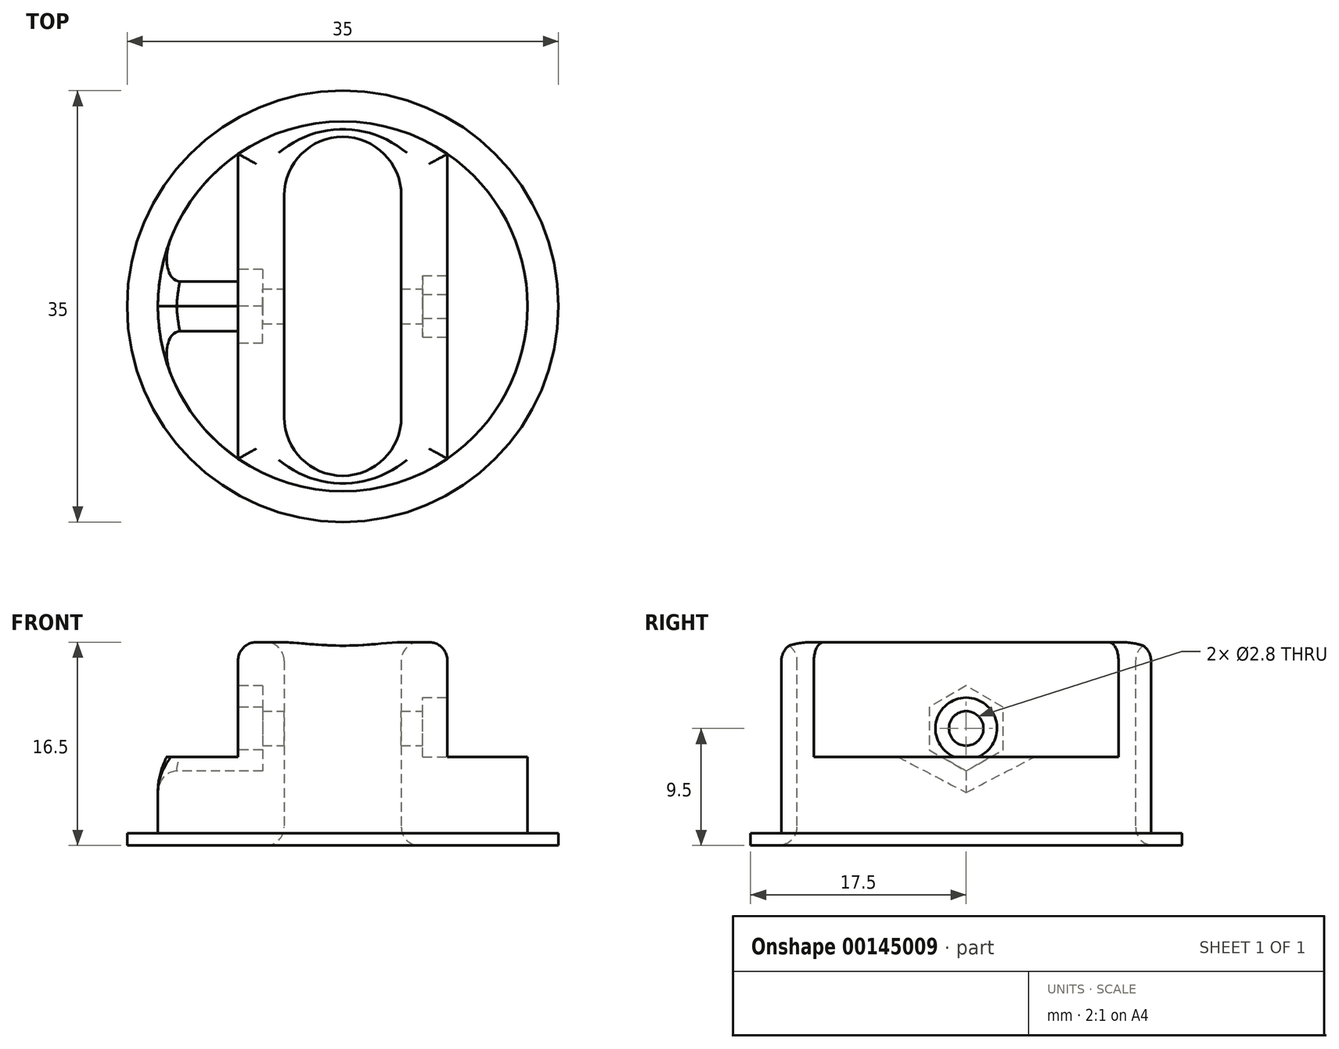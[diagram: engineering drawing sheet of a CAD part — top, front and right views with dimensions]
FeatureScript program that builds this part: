
annotation { "Feature Type Name" : "Feature", "Feature Type Description" : "" }
export const myFeature = defineFeature(function(context is Context, id is Id, definition is map)
    precondition{}
    {
        {
            var Q0;
            Q0=qCreatedBy(makeId("Top.planeOp"),FACE);
            var sketch = newSketch(context, id + "F0", { "sketchPlane" : qUnion([Q0])});
            skCircle(sketch, "E0", {"center": v(0, 0) * mm, "radius": 17.5 * mm});
            skCircle(sketch, "E1", {"center": v(0, 0) * mm, "radius": 15 * mm});
            skLineSegment(sketch, "E2.bottom", {"start": v(4.75, 9) * mm, "end": v(-4.75, 9) * mm, "construction": true});
            skLineSegment(sketch, "E2.top", {"start": v(4.75, -9) * mm, "end": v(-4.75, -9) * mm, "construction": true});
            skLineSegment(sketch, "E2.left", {"start": v(4.75, 9) * mm, "end": v(4.75, -9) * mm});
            skLineSegment(sketch, "E2.right", {"start": v(-4.75, 9) * mm, "end": v(-4.75, -9) * mm});
            skArc(sketch, "E3", {"start": v(4.75, 9) * mm, "mid": v(0, 13.75) * mm, "end": v(-4.75, 9) * mm});
            skArc(sketch, "E4", {"start": v(-4.75, -9) * mm, "mid": v(0, -13.75) * mm, "end": v(4.75, -9) * mm});
            skLineSegment(sketch, "E5.bottom", {"start": v(3.5, 11.5) * mm, "end": v(-3.5, 11.5) * mm, "construction": true});
            skLineSegment(sketch, "E5.top", {"start": v(3.5, -11.5) * mm, "end": v(-3.5, -11.5) * mm, "construction": true});
            skLineSegment(sketch, "E5.left", {"start": v(3.5, 11.5) * mm, "end": v(3.5, -11.5) * mm, "construction": true});
            skLineSegment(sketch, "E5.right", {"start": v(-3.5, 11.5) * mm, "end": v(-3.5, -11.5) * mm, "construction": true});
            skSolve(sketch);
        }
        {
            var Q0;
            Q0=makeQuery(id+"F0.imprint","IMPRINT",FACE,{"disambiguationData":[TD([[makeQuery(id+"F0.imprint","IMPRINT",EDGE,{"derivedFrom":sQuery(id+"F0.wireOp",EDGE,"E0")}),1.0]])]});
            extrude(context, id + "F1", {"entities" : qUnion([Q0]), "depth" : 1 * mm});
        }
        {
            var Q0;
            Q0=makeQuery(id+"F0.imprint","IMPRINT",FACE,{"disambiguationData":[TD([[makeQuery(id+"F0.imprint","IMPRINT",EDGE,{"derivedFrom":sQuery(id+"F0.wireOp",EDGE,"E1")}),1.0]])]});
            extrude(context, id + "F2", {"entities" : qUnion([Q0]), "operationType" : NewBodyOperationType.ADD, "depth" : 16.5 * mm});
        }
        {
            var Q0;
            Q0=makeQuery(id+"F2.opExtrude","CAP_FACE",FACE,{"disambiguationData":[OSD([sQuery(id+"F0.wireOp",EDGE,"E1"),sQuery(id+"F0.wireOp",EDGE,"E2.left"),sQuery(id+"F0.wireOp",EDGE,"E2.right"),sQuery(id+"F0.wireOp",EDGE,"E3"),sQuery(id+"F0.wireOp",EDGE,"E4")])],"isStart":false});
            var sketch = newSketch(context, id + "F3", { "sketchPlane" : qUnion([Q0])});
            skLineSegment(sketch, "E6.bottom", {"start": v(-8.5, 22.5) * mm, "end": v(8.5, 22.5) * mm});
            skLineSegment(sketch, "E6.top", {"start": v(-8.5, -22.5) * mm, "end": v(8.5, -22.5) * mm});
            skLineSegment(sketch, "E6.left", {"start": v(-8.5, 22.5) * mm, "end": v(-8.5, -22.5) * mm});
            skLineSegment(sketch, "E6.right", {"start": v(8.5, 22.5) * mm, "end": v(8.5, -22.5) * mm});
            skPoint(sketch, "E6.middle", {"position": v(0, 0) * mm});
            skCircle(sketch, "E7.0", {"center": v(0, 0) * mm, "radius": 15 * mm});
            skSolve(sketch);
        }
        {
            var Q0;
            {var subQ0=sQuery(id+"F3.wireOp",EDGE,"E7.0");var subQ1=sQuery(id+"F3.wireOp",EDGE,"E6.left");var subQ2=makeQuery(id+"F3.imprint","INTERSECT",VERTEX,{"disambiguationData":[OD(0.0)],"derivedFrom":[subQ1,subQ0]});Q0=makeQuery(id+"F3.imprint","IMPRINT",FACE,{"disambiguationData":[TD([[makeQuery(id+"F3.imprint","IMPRINT",EDGE,{"disambiguationData":[TD([[subQ2,-1.0]])],"derivedFrom":subQ1}),-1.0]])]});}
            var Q1;
            {var subQ0=sQuery(id+"F3.wireOp",EDGE,"E7.0");var subQ1=sQuery(id+"F3.wireOp",EDGE,"E6.right");var subQ2=makeQuery(id+"F3.imprint","INTERSECT",VERTEX,{"disambiguationData":[OD(0.0)],"derivedFrom":[subQ1,subQ0]});Q1=makeQuery(id+"F3.imprint","IMPRINT",FACE,{"disambiguationData":[TD([[makeQuery(id+"F3.imprint","IMPRINT",EDGE,{"disambiguationData":[TD([[subQ2,-1.0]])],"derivedFrom":subQ1}),1.0]])]});}
            extrude(context, id + "F4", {"entities" : qUnion([Q0, Q1]), "operationType" : NewBodyOperationType.REMOVE, "oppositeDirection" : true, "depth" : 9.3 * mm});
        }
        {
            var Q0;
            Q0=makeQuery(id+"F4.boolean.opBoolean","COPY",FACE,{"derivedFrom":makeQuery(id+"F4.opExtrude","SWEPT_FACE",FACE,{"disambiguationData":[OSD([sQuery(id+"F3.wireOp",EDGE,"E6.right")])]})});
            var sketch = newSketch(context, id + "F5", { "sketchPlane" : qUnion([Q0])});
            skLineSegment(sketch, "E8", {"start": v(0, 16.5) * mm, "end": v(0, 7.2) * mm, "construction": true});
            skCircle(sketch, "E9", {"center": v(0, 9.5) * mm, "radius": 1.4 * mm});
            skCircle(sketch, "E10", {"center": v(0, 9.5) * mm, "radius": 2.5 * mm});
            skSolve(sketch);
        }
        {
            var Q0;
            Q0=makeQuery(id+"F5.imprint","IMPRINT",FACE,{"disambiguationData":[TD([[makeQuery(id+"F5.imprint","IMPRINT",EDGE,{"derivedFrom":sQuery(id+"F5.wireOp",EDGE,"E9")}),1.0]])]});
            extrude(context, id + "F6", {"entities" : qUnion([Q0]), "operationType" : NewBodyOperationType.REMOVE, "endBound" : BoundingType.THROUGH_ALL, "oppositeDirection" : true, "depth" : 25 * mm});
        }
        {
            var Q0;
            Q0=makeQuery(id+"F5.imprint","IMPRINT",FACE,{"disambiguationData":[TD([[makeQuery(id+"F5.imprint","IMPRINT",EDGE,{"derivedFrom":sQuery(id+"F5.wireOp",EDGE,"E9")}),-1.0]])]});
            extrude(context, id + "F7", {"entities" : qUnion([Q0]), "operationType" : NewBodyOperationType.REMOVE, "oppositeDirection" : true, "depth" : 2 * mm});
        }
        {
            var Q0;
            Q0=makeQuery(id+"F4.boolean.opBoolean","COPY",FACE,{"derivedFrom":makeQuery(id+"F4.opExtrude","SWEPT_FACE",FACE,{"disambiguationData":[OSD([sQuery(id+"F3.wireOp",EDGE,"E6.left")])]})});
            var sketch = newSketch(context, id + "F8", { "sketchPlane" : qUnion([Q0])});
            skCircle(sketch, "E11.cCircle", {"center": v(0, 9.5) * mm, "radius": 3 * mm, "construction": true});
            skLineSegment(sketch, "E11.0", {"start": v(3, 11.23) * mm, "end": v(3, 7.77) * mm});
            skLineSegment(sketch, "E11.1", {"start": v(3, 7.77) * mm, "end": v(0, 6.04) * mm});
            skLineSegment(sketch, "E11.2", {"start": v(0, 6.04) * mm, "end": v(-3, 7.77) * mm});
            skLineSegment(sketch, "E11.3", {"start": v(-3, 7.77) * mm, "end": v(-3, 11.23) * mm});
            skLineSegment(sketch, "E11.4", {"start": v(-3, 11.23) * mm, "end": v(0, 12.96) * mm});
            skLineSegment(sketch, "E11.5", {"start": v(0, 12.96) * mm, "end": v(3, 11.23) * mm});
            skPoint(sketch, "E11.0.midPoint", {"position": v(3, 9.5) * mm});
            skSolve(sketch);
        }
        {
            var Q0;
            {var subQ7=sQuery(id+"F8.wireOp",EDGE,"E11.0");Q0=makeQuery(id+"F8.imprint","IMPRINT",FACE,{"disambiguationData":[TD([[makeQuery(id+"F8.imprint","IMPRINT",EDGE,{"derivedFrom":subQ7}),-1.0]])]});}
            var Q1;
            {var subQ0=sQuery(id+"F8.wireOp",EDGE,"E11.2");var subQ1=sQuery(id+"F8.wireOp",EDGE,"E11.1");var subQ2=makeQuery(id+"F8.imprint","INTERSECT",VERTEX,{"derivedFrom":[subQ1,subQ0]});Q1=makeQuery(id+"F8.imprint","IMPRINT",FACE,{"disambiguationData":[TD([[makeQuery(id+"F8.imprint","IMPRINT",EDGE,{"disambiguationData":[TD([[subQ2,1.0]])],"derivedFrom":subQ1}),-1.0]])]});}
            extrude(context, id + "F9", {"entities" : qUnion([Q0, Q1]), "operationType" : NewBodyOperationType.REMOVE, "oppositeDirection" : true, "depth" : 2 * mm});
        }
        {
            var Q0;
            Q0=makeQuery(id+"F9.boolean.opBoolean","COPY",FACE,{"derivedFrom":makeQuery(id+"F9.opExtrude","CAP_FACE",FACE,{"disambiguationData":[OSD([sQuery(id+"F3.wireOp",EDGE,"E6.left"),sQuery(id+"F5.wireOp",EDGE,"E9"),sQuery(id+"F8.wireOp",EDGE,"E11.0"),sQuery(id+"F8.wireOp",EDGE,"E11.1"),sQuery(id+"F8.wireOp",EDGE,"E11.2"),sQuery(id+"F8.wireOp",EDGE,"E11.3"),sQuery(id+"F8.wireOp",EDGE,"E11.4"),sQuery(id+"F8.wireOp",EDGE,"E11.5")])],"isStart":false})});
            var sketch = newSketch(context, id + "F10", { "sketchPlane" : qUnion([Q0])});
            skCircle(sketch, "E12.cCircle", {"center": v(0, 9.5) * mm, "radius": 3 * mm, "construction": true});
            skLineSegment(sketch, "E12.0", {"start": v(-3, 7.77) * mm, "end": v(-3, 11.23) * mm});
            skLineSegment(sketch, "E12.1", {"start": v(-3, 11.23) * mm, "end": v(0, 12.96) * mm});
            skLineSegment(sketch, "E12.2", {"start": v(0, 12.96) * mm, "end": v(3, 11.23) * mm});
            skLineSegment(sketch, "E12.3", {"start": v(3, 11.23) * mm, "end": v(3, 7.77) * mm});
            skLineSegment(sketch, "E12.4", {"start": v(3, 7.77) * mm, "end": v(0, 6.04) * mm});
            skLineSegment(sketch, "E12.5", {"start": v(0, 6.04) * mm, "end": v(-3, 7.77) * mm});
            skPoint(sketch, "E12.0.midPoint", {"position": v(-3, 9.5) * mm});
            skSolve(sketch);
        }
        {
            var Q0;
            Q0=makeQuery(id+"F10.imprint","IMPRINT",FACE,{"disambiguationData":[TD([[makeQuery(id+"F10.imprint","IMPRINT",EDGE,{"derivedFrom":sQuery(id+"F10.wireOp",EDGE,"E12.0")}),-1.0]])]});
            extrude(context, id + "F11", {"entities" : qUnion([Q0]), "operationType" : NewBodyOperationType.REMOVE, "depth" : 25 * mm});
        }
        {
            var Q0;
            Q0=makeQuery(id+"F2.opExtrude","CAP_FACE",FACE,{"disambiguationData":[OSD([sQuery(id+"F0.wireOp",EDGE,"E1"),sQuery(id+"F0.wireOp",EDGE,"E2.left"),sQuery(id+"F0.wireOp",EDGE,"E2.right"),sQuery(id+"F0.wireOp",EDGE,"E3"),sQuery(id+"F0.wireOp",EDGE,"E4")])],"isStart":false});
            var Q1;
            {var subQ0=sQuery(id+"F3.wireOp",EDGE,"E7.0");var subQ1=sQuery(id+"F3.wireOp",EDGE,"E6.right");Q1=makeQuery(id+"F4.boolean.opBoolean","COPY",EDGE,{"derivedFrom":makeQuery(id+"F4.opExtrude","CAP_EDGE",EDGE,{"disambiguationData":[OSD([subQ0]),TDD([makeQuery(id+"F3.imprint","IMPRINT",EDGE,{"disambiguationData":[TD([[makeQuery(id+"F3.imprint","INTERSECT",VERTEX,{"disambiguationData":[OD(0.0)],"derivedFrom":[subQ1,subQ0]}),1.0]])],"derivedFrom":subQ0})])],"isStart":false})});}
            var Q2;
            {var subQ0=sQuery(id+"F3.wireOp",EDGE,"E7.0");var subQ1=sQuery(id+"F3.wireOp",EDGE,"E6.left");Q2=makeQuery(id+"F11.boolean.opBoolean","SPLIT",EDGE,{"disambiguationData":[TD([makeQuery(id+"F9.boolean.opBoolean","COPY",FACE,{"derivedFrom":makeQuery(id+"F9.opExtrude","SWEPT_FACE",FACE,{"disambiguationData":[OSD([sQuery(id+"F8.wireOp",EDGE,"E11.1")])]})})])],"derivedFrom":makeQuery(id+"F4.boolean.opBoolean","COPY",EDGE,{"derivedFrom":makeQuery(id+"F4.opExtrude","CAP_EDGE",EDGE,{"disambiguationData":[OSD([subQ0]),TDD([makeQuery(id+"F3.imprint","IMPRINT",EDGE,{"disambiguationData":[TD([[makeQuery(id+"F3.imprint","INTERSECT",VERTEX,{"disambiguationData":[OD(0.0)],"derivedFrom":[subQ1,subQ0]}),-1.0]])],"derivedFrom":subQ0})])],"isStart":false})})});}
            var Q3;
            {var subQ0=sQuery(id+"F3.wireOp",EDGE,"E7.0");var subQ1=sQuery(id+"F3.wireOp",EDGE,"E6.left");Q3=makeQuery(id+"F11.boolean.opBoolean","SPLIT",EDGE,{"disambiguationData":[TD([makeQuery(id+"F9.boolean.opBoolean","COPY",FACE,{"derivedFrom":makeQuery(id+"F9.opExtrude","SWEPT_FACE",FACE,{"disambiguationData":[OSD([sQuery(id+"F8.wireOp",EDGE,"E11.2")])]})})])],"derivedFrom":makeQuery(id+"F4.boolean.opBoolean","COPY",EDGE,{"derivedFrom":makeQuery(id+"F4.opExtrude","CAP_EDGE",EDGE,{"disambiguationData":[OSD([subQ0]),TDD([makeQuery(id+"F3.imprint","IMPRINT",EDGE,{"disambiguationData":[TD([[makeQuery(id+"F3.imprint","INTERSECT",VERTEX,{"disambiguationData":[OD(0.0)],"derivedFrom":[subQ1,subQ0]}),-1.0]])],"derivedFrom":subQ0})])],"isStart":false})})});}
            var Q4;
            Q4=makeQuery(id+"F11.boolean.opBoolean","INTERSECT",EDGE,{"derivedFrom":[makeQuery(id+"F2.opExtrude","SWEPT_FACE",FACE,{"disambiguationData":[OSD([sQuery(id+"F0.wireOp",EDGE,"E1")])]}),makeQuery(id+"F11.opExtrude","SWEPT_FACE",FACE,{"disambiguationData":[OSD([sQuery(id+"F10.wireOp",EDGE,"E12.5")])]})]});
            var Q5;
            Q5=makeQuery(id+"F11.boolean.opBoolean","INTERSECT",EDGE,{"derivedFrom":[makeQuery(id+"F2.opExtrude","SWEPT_FACE",FACE,{"disambiguationData":[OSD([sQuery(id+"F0.wireOp",EDGE,"E1")])]}),makeQuery(id+"F11.opExtrude","SWEPT_FACE",FACE,{"disambiguationData":[OSD([sQuery(id+"F10.wireOp",EDGE,"E12.4")])]})]});
            var Q6;
            Q6=makeQuery(id+"F2.opExtrude","CAP_EDGE",EDGE,{"disambiguationData":[OSD([sQuery(id+"F0.wireOp",EDGE,"E2.left")])],"isStart":true});
            fillet(context, id + "F12", {"entities" : qUnion([Q0, Q1, Q2, Q3, Q4, Q5, Q6]), "radius" : 1.5 * mm, "tangentPropagation" : true, "allowEdgeOverflow" : false});
        }
    });
